# Revit family: R SONNIGER - Nagrzewnica wodna HEATER - MIX 1, MIX 2
name_source: partatom
category: Wyposażenie mechaniczne
revit_build: Autodesk Revit 2018 (Build: 20170927_1515(x64)
units: mm (PartAtom-declared; Revit-internal decimal feet)

## family parameters
Klasyfikacja = Brak
Obiekt nadrzędny = Powierzchnia
Punkt obliczania pomieszczeń = Nie
Tnij formami wycięć po wczytaniu = Nie
Typ części = Normalny
Współdzielony = Nie
Wymiar okrągłego złącza = Użyj średnicy

## types (2) — shared parameters
Domyślna rzędna = 1219.200 mm
O = 130.000 mm
Producent = SONNIGER Polska Sp. z o.o. Sp. k.
автор = www.archispace.com
класс IP = IP54
максимальная высота установки = 15.000 mm
максимальная площадь покрытия = 380 m²
материал = 230,230,230
минимальный высота установки = 9.000 mm
минимальный площадь покрытия = 200 m²
напряжение питания = 230 V
zero-valued in all types: Уровень шума

## per-type parameters (varying)
| type | H | Model | O1 | Opis | S g | W g | Масса оборудования | Мощность электродвигателя | максимальный расход воздуха | масса оборудования с водой | уровень шума | частота вращения двигателя |
| MIX 1 - настенный монтаж | 13536.341 mm | Mix 1 | Tak | Дестратификатор Heater MIX 1 | 19500.000 mm | 19500.000 mm | 9.20 kg | 250 W | 4800.0 m³/h | 9.20 kg | I bieg 36 dB / II bieg 44 dB / III bieg 54 dB | 1350 |
| MIX 2 - настенный монтаж | 16560.341 mm | Mix 2 | Nie | Дестратификатор Heater MIX 2 | 21200.000 mm | 21200.000 mm | 15.80 kg | 520 W | 7200.0 m³/h | 15.80 kg | I скорость 31 dB / II скорость 42 dB / III скорость 49 dB | 1380 |
